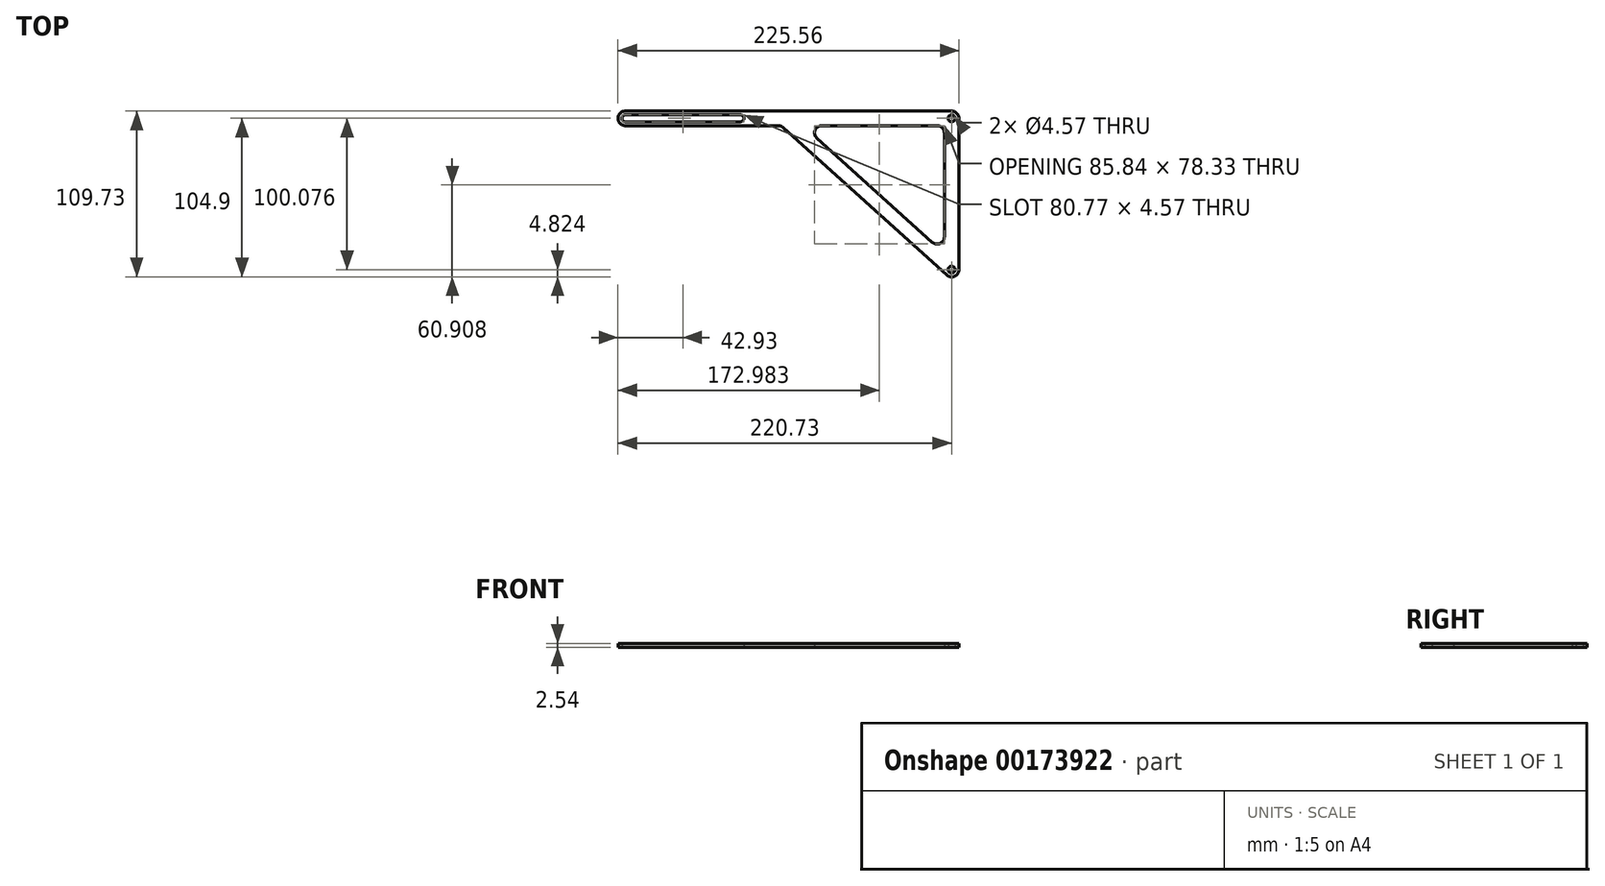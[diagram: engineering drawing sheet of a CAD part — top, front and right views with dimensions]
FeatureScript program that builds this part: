
annotation { "Feature Type Name" : "Feature", "Feature Type Description" : "" }
export const myFeature = defineFeature(function(context is Context, id is Id, definition is map)
    precondition{}
    {
        {
            var Q0;
            Q0=qCreatedBy(makeId("Top.planeOp"),FACE);
            var sketch = newSketch(context, id + "F0", { "sketchPlane" : qUnion([Q0])});
            skCircle(sketch, "E0", {"center": v(0, 0) * mm, "radius": 2.29 * mm});
            skCircle(sketch, "E1", {"center": v(0, -100.08) * mm, "radius": 2.29 * mm});
            skArc(sketch, "E2", {"start": v(-215.9, 2.29) * mm, "mid": v(-218.19, 0) * mm, "end": v(-215.9, -2.29) * mm});
            skArc(sketch, "E3", {"start": v(-139.7, -2.29) * mm, "mid": v(-137.41, 0) * mm, "end": v(-139.7, 2.29) * mm});
            skLineSegment(sketch, "E4", {"start": v(-215.9, 2.29) * mm, "end": v(-139.7, 2.29) * mm});
            skLineSegment(sketch, "E5", {"start": v(-139.7, -2.29) * mm, "end": v(-215.9, -2.29) * mm});
            skLineSegment(sketch, "E6", {"start": v(-215.9, 4.83) * mm, "end": v(0, 4.83) * mm});
            skLineSegment(sketch, "E7", {"start": v(4.83, 0) * mm, "end": v(4.83, -100.08) * mm});
            skArc(sketch, "E8", {"start": v(4.83, 0) * mm, "mid": v(3.41, 3.41) * mm, "end": v(0, 4.83) * mm});
            skArc(sketch, "E9", {"start": v(-215.9, 4.83) * mm, "mid": v(-220.73, 0) * mm, "end": v(-215.9, -4.83) * mm});
            skLineSegment(sketch, "E10", {"start": v(-215.9, -4.83) * mm, "end": v(-114.68, -4.83) * mm});
            skLineSegment(sketch, "E11", {"start": v(-111.44, -6.07) * mm, "end": v(-3.23, -103.66) * mm});
            skArc(sketch, "E12", {"start": v(-3.23, -103.66) * mm, "mid": v(1.96, -104.49) * mm, "end": v(4.83, -100.08) * mm});
            skArc(sketch, "E13", {"start": v(-111.44, -6.07) * mm, "mid": v(-112.94, -5.15) * mm, "end": v(-114.68, -4.83) * mm});
            skLineSegment(sketch, "E14", {"start": v(-89.08, -13.24) * mm, "end": v(-12.88, -81.96) * mm});
            skLineSegment(sketch, "E15", {"start": v(-85.85, -4.83) * mm, "end": v(-9.65, -4.83) * mm});
            skLineSegment(sketch, "E16", {"start": v(-4.83, -4.83) * mm, "end": v(-4.83, -9.65) * mm, "construction": true});
            skLineSegment(sketch, "E17", {"start": v(-4.83, -4.83) * mm, "end": v(4.83, -4.83) * mm, "construction": true});
            skLineSegment(sketch, "E18", {"start": v(-215.9, 4.83) * mm, "end": v(-215.9, -4.83) * mm, "construction": true});
            skLineSegment(sketch, "E19", {"start": v(-4.83, -4.83) * mm, "end": v(-4.83, 4.83) * mm, "construction": true});
            skArc(sketch, "E20", {"start": v(-85.85, -4.83) * mm, "mid": v(-90.36, -7.92) * mm, "end": v(-89.08, -13.24) * mm});
            skArc(sketch, "E21", {"start": v(-12.88, -81.96) * mm, "mid": v(-7.7, -82.78) * mm, "end": v(-4.83, -78.37) * mm});
            skLineSegment(sketch, "E22", {"start": v(-89.08, -13.24) * mm, "end": v(-95.55, -20.4) * mm, "construction": true});
            skLineSegment(sketch, "E23", {"start": v(-9.65, -4.83) * mm, "end": v(-4.83, -4.83) * mm, "construction": true});
            skLineSegment(sketch, "E24", {"start": v(-4.83, -9.65) * mm, "end": v(-4.83, -78.37) * mm});
            skArc(sketch, "E25", {"start": v(-4.83, -9.65) * mm, "mid": v(-6.24, -6.24) * mm, "end": v(-9.65, -4.83) * mm});
            skSolve(sketch);
        }
        {
            var Q0;
            Q0 = qSketchRegion(id + "F0", true);
            extrude(context, id + "F1", {"entities" : qUnion([Q0]), "depth" : 2.54 * mm});
        }
    });
